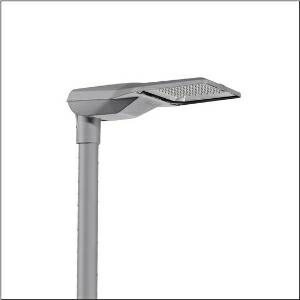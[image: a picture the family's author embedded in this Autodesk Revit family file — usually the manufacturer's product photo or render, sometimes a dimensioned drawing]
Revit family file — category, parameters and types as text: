
# Revit family: streetlight_sl_21_iq_midi___st0_5a_5xe3b41g08nb_d4f3
name_source: partatom
category: Lighting Fixtures
units: mm (PartAtom-declared; Revit-internal decimal feet)

## family parameters
Cut with Voids When Loaded = No
Host = Face
Light Source = No
Part Type = Normal
Room Calculation Point = No
Round Connector Dimension = Use Diameter
Shared = No

## types (1)
- --- (1 x LED, 24250 lm, 155.5 W, 4000K)
    Apparent Load = 155 VA
    CIE Flux Codes = 43 76 97 100 100
    Color Rendering = 70
    Color Temperature = 4000K
    Default Elevation = 1800 mm
    Description = Streetlight SL 21 iQ midi, mast luminaire, primary light control with lens, of PMMA, primary optical cover: cover, of toughened safety glass, transparent, light distribution: ST0.5a, light emission: direct distribution, primary light characteristic: asymmetric, installation type: post-top, side-entry, LED, High Power LED, rated luminous flux: 24.250lm, luminous efficacy: 156lm/W, light colour: 740, colour temperature: 4000K, control gear: iQ Street-Remote, control: Street-Remote, Auto-Match, Temp-Guard, Lumen-Switch, Night-Set, Smart-Wire, Light-Fading, Desk-Remote (wireless, voltage-free reading and setting of iQ features in the workshop via application-optimized NFC function/RFID function), optimised constant luminous flux control (CLO 2.0), pre-setting: linear dimming characteristic, mains connection: 230..240V, AC, 50/60Hz, start of lifetime: 156W, end of service life: 162W, reduction: 69W, luminaire housing, of diecast aluminium, powder-coated, Siteco® metallic grey (DB 702S), corrosivity category C5 mid according to DIN EN ISO 12944, please order mast flange separately, inclination adjustable: 0°, 5°, 10°, 15°, sealing non-destructively replaceable, multi-level sealing system, length: 644mm, width: 335mm, height: 110mm, mast flange for spigot size: 42mm (side-entry): 5XC10008XM4, 60/48mm (side-entry/post-top): 5XC10108XM2, 76/60mm (side-entry/post-top): 5XC10108XM1, mounting height: 4..8m, protection rating (complete): IP66, insulation class (complete): insulation class II (safety insulation), certification: CE, ENEC, ENEC+, VDE, impact resistance: IK10, permissible operating ambient temperature for outdoor applications: -40..+50°C, standard-compliant lighting for roads and squares, packaging unit: 1 piece

Light Distribution: ST0.5a
    Height = 111 mm
    Lamp = 1 x LED
    Lamp Light Flux = 24250 lm
    Lamp Power = 155.5 W
    Lamp count = 1
    Length = 644 mm
    Luminous efficacy = 156 lm/W
    Manufacturer = Siteco
    ModVariant = No
    Model = 5XE3B41G08NB
    Number of Poles = 1
    OnlyDefault = Yes
    Power Factor = 1
    Product Name = Streetlight SL 21 iQ midi | ST0.5a
    Product group = mast luminaire | pylon top
    ProductGroupID = 6100
    Protection Class = Protection class II
    Protection Degree = IP 66
    RLX_Detail_Level = 1
    RLX_Emergency_Light_Flux = 0 lm
    RLX_Emergency_Type = 0
    RLX_Emergency_Type_DB = No
    RlxData = <blob elided: 38321 chars, md5=863b9de9>
    Socket = socket
    Standby Power = 0 W
    System Light Flux = 24250 lm
    System Power = 155 W
    Type Comments = factory setting: luminous flux: 100 % | dim-lin: 254 | 823 mA
    Type Image = l_1004298.jpg
    URL = http://relux.com
    VarID = @adj_192931
    Voltage = 0 V
    Weight = 0.00 kg
    Width = 336 mm

## geometry (parser evidence)
native form markers: Blend x4, Sweep x9
no freeform markers — native parametric forms only
